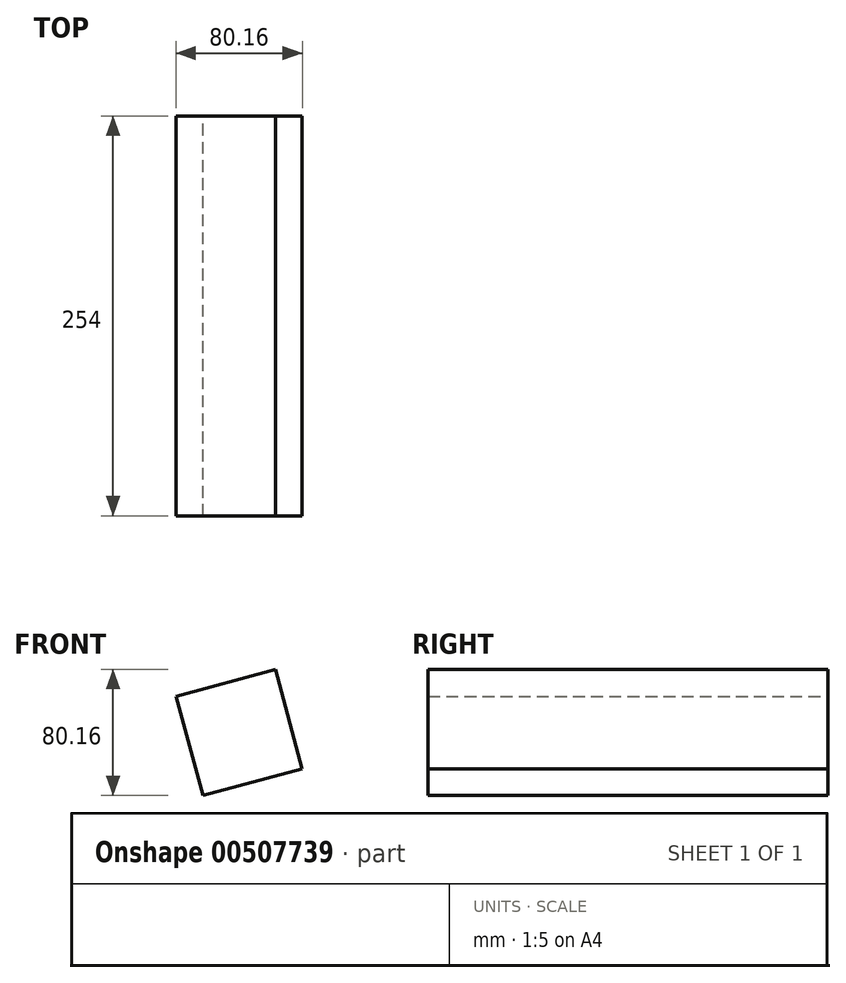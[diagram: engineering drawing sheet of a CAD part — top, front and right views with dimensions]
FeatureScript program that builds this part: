
annotation { "Feature Type Name" : "Feature", "Feature Type Description" : "" }
export const myFeature = defineFeature(function(context is Context, id is Id, definition is map)
    precondition{}
    {
        {
            var Q0;
            Q0=qCreatedBy(makeId("Front.planeOp"),FACE);
            var sketch = newSketch(context, id + "F0", { "sketchPlane" : qUnion([Q0])});
            skCircle(sketch, "E0.cCircle", {"center": v(0, 0) * mm, "radius": 46.22 * mm, "construction": true});
            skLineSegment(sketch, "E0.0", {"start": v(23.03, 40.08) * mm, "end": v(40.08, -23.03) * mm});
            skLineSegment(sketch, "E0.1", {"start": v(40.08, -23.03) * mm, "end": v(-23.03, -40.08) * mm});
            skLineSegment(sketch, "E0.2", {"start": v(-23.03, -40.08) * mm, "end": v(-40.08, 23.03) * mm});
            skLineSegment(sketch, "E0.3", {"start": v(-40.08, 23.03) * mm, "end": v(23.03, 40.08) * mm});
            skSolve(sketch);
        }
        {
            var Q0;
            Q0=makeQuery(id+"F0.imprint","IMPRINT",FACE,{"disambiguationData":[TD([[makeQuery(id+"F0.imprint","IMPRINT",EDGE,{"derivedFrom":sQuery(id+"F0.wireOp",EDGE,"E0.0")}),-1.0]])]});
            extrude(context, id + "F1", {"entities" : qUnion([Q0]), "depth" : 254 * mm});
        }
    });
